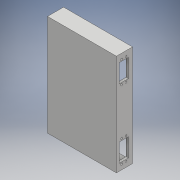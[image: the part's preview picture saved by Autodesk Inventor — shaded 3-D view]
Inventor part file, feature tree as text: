
AUTODESK INVENTOR PART (.ipt)
format: ipt  version: 2018 (Build 220112000, 112)  size: 169,472 bytes
history: native  units: mm
features: other x6, extrude x4, sketch x4
ambient origin geometry x8: Origin, YZ Plane, XZ Plane, XY Plane, X Axis, Y Axis, Z Axis, Center Point
bodies: Solid1 (feature_tree)
feature tree (14):
  other  "Blocks"
  extrude  "Extrusion1"  Depth=220.0mm
  extrude  "Extrusion2"  Depth=5.0mm
  sketch  "Sketch4"  dims[d5=5.0mm d6=5.0mm]
  sketch  "Sketch5"  dims[d7=5.0mm d8=30.0mm d9=0.0mm d10=8.0mm d11=6.0mm d12=8.0mm d13=6.0mm d14=6.0mm d15=8.0mm d16=6.0mm d17=8.0mm d18=5.0mm d19=0.0mm d20=5.0mm d21=0.0mm]
  extrude  "Extrusion3"  Depth=5.0mm
  extrude  "Extrusion4"  Depth=30.0mm TaperAngle=0.0deg
  sketch  "Sketch1"  dims[d0=150.0mm d1=220.0mm]
  sketch  "Sketch3"  dims[d2=5.0mm d3=0.0mm d4=5.0mm]
  other  "servo"
  other  "servo:1"
  other  "servo:2"
  other  "servo:3"
  other  "servo:4"
